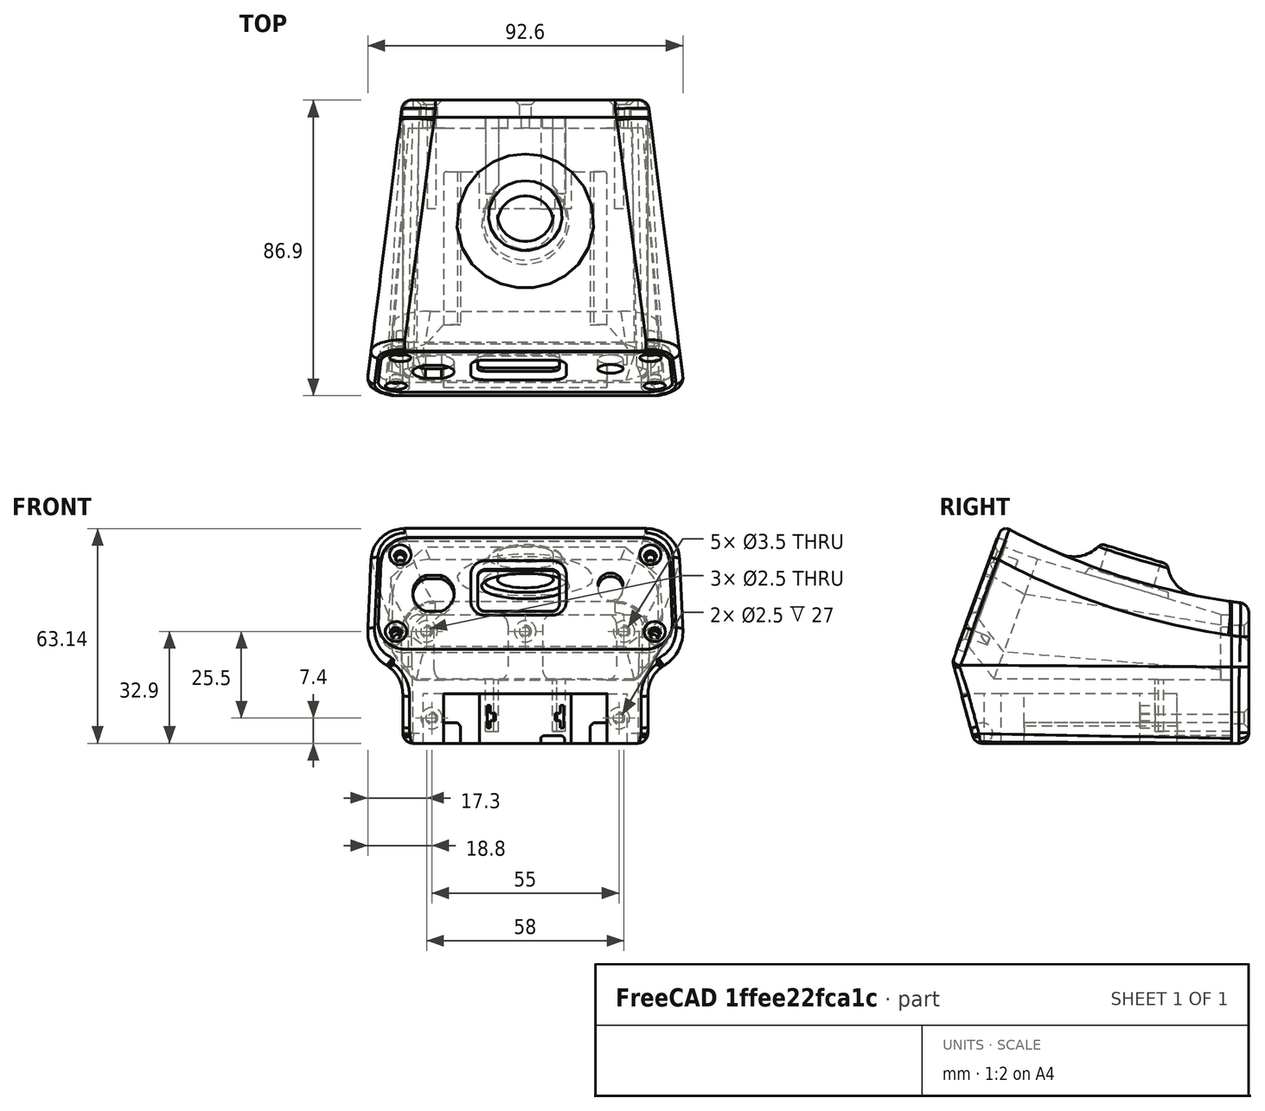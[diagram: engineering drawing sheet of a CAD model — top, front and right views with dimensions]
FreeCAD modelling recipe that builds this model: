
FCSTD DOCUMENT  (FreeCAD 2022.709R28846 (Git))
Label: solder_station4_snap
License: All rights reserved
LicenseURL: http://en.wikipedia.org/wiki/All_rights_reserved
objects: Sketcher::SketchObject×19, PartDesign::Pocket×9, PartDesign::Fillet×6, Mesh::Feature×4, Part::FeaturePython×3, App::DocumentObjectGroup×3, PartDesign::Chamfer×3, PartDesign::Body×3, PartDesign::FeatureBase×2, PartDesign::Pad×2, Spreadsheet::Sheet×1, Part::Plane×1, Part::Loft×1, Part::Extrusion×1, Part::MultiCommon×1, PartDesign::SubtractiveLoft×1, PartDesign::Revolution×1, PartDesign::Groove×1, App::Part×1
note: 102 computed .brp shape members not serialized (recipe doc carries the construction recipe); baked Part::Feature solids carry a one-line shape summary decoded from their .brp

FEATURE [Sketcher::SketchObject] Sketch  label="RearSupport"
  ArcFitTolerance = 0
  AttachmentOffset = pos=(0,0,-37.8) rot=(0,0,1;0rad)
  AttachmentSupport = -> [XZ_Plane005]
  FullyConstrained = true
  MapMode = 5
  Placement = pos=(0,37.8,8.4e-15) rot=(1,0,0;1.5708rad)
  Support = -> [XZ_Plane005]
  TreeRank = 0
  expr: AttachmentOffset.Base.z = -<<param>>.mid_depth / 2 + <<param>>.wall
  expr: Constraints[24] = 3
  expr: Constraints[37] = <<param>>.bottom_height
  expr: Constraints[38] = <<param>>.floor
  expr: Constraints[39] = <<param>>.rear_height - <<param>>.wall
  expr: Constraints[47] = <<param>>.reart_screw_width2
  expr: Constraints[48] = <<param>>.rear_screw_width1
  expr: Constraints[49] = <<param>>.screw_hole
  expr: Constraints[50] = <<param>>.rear_screw_height
  expr: Constraints[51] = <<param>>.rear_screw_height
  expr: Constraints[52] = <<param>>.rear_screw_offset
  sketch-geometry (22):
    g0: LineSegment StartX=-23.8 StartY=13.8 StartZ=0 EndX=-8.1 EndY=13.8 EndZ=0
    g1: LineSegment StartX=26.8 StartY=10.8 StartZ=0 EndX=26.8 EndY=-2.4 EndZ=0
    g2: LineSegment StartX=23.8 StartY=-5.4 StartZ=0 EndX=8.1 EndY=-5.4 EndZ=0
    g3: LineSegment StartX=-26.8 StartY=-2.4 StartZ=0 EndX=-26.8 EndY=10.8 EndZ=0
    g4: LineSegment StartX=-5.1 StartY=10.8 StartZ=0 EndX=-5.1 EndY=-2.4 EndZ=0
    g5: LineSegment StartX=5.1 StartY=10.8 StartZ=0 EndX=5.1 EndY=-2.4 EndZ=0
    g6: LineSegment StartX=8.1 StartY=13.8 StartZ=0 EndX=23.8 EndY=13.8 EndZ=0
    g7: LineSegment StartX=-8.1 StartY=-5.4 StartZ=0 EndX=-23.8 EndY=-5.4 EndZ=0
    g8: ArcOfCircle CenterX=-8.1 CenterY=10.8 CenterZ=0 NormalX=0 NormalY=0 NormalZ=1 AngleXU=0 Radius=3 StartAngle=0 EndAngle=1.5708
    g9: ArcOfCircle CenterX=8.1 CenterY=10.8 CenterZ=0 NormalX=0 NormalY=0 NormalZ=1 AngleXU=0 Radius=3 StartAngle=1.5708 EndAngle=3.14159
    g10: ArcOfCircle CenterX=-8.1 CenterY=-2.4 CenterZ=0 NormalX=0 NormalY=0 NormalZ=1 AngleXU=0 Radius=3 StartAngle=4.71239 EndAngle=6.28319
    g11: ArcOfCircle CenterX=8.1 CenterY=-2.4 CenterZ=0 NormalX=0 NormalY=0 NormalZ=1 AngleXU=0 Radius=3 StartAngle=3.14159 EndAngle=4.71239
    g12: ArcOfCircle CenterX=-23.8 CenterY=10.8 CenterZ=0 NormalX=0 NormalY=0 NormalZ=1 AngleXU=0 Radius=3 StartAngle=1.5708 EndAngle=3.14159
    g13: ArcOfCircle CenterX=-23.8 CenterY=-2.4 CenterZ=0 NormalX=0 NormalY=0 NormalZ=1 AngleXU=0 Radius=3 StartAngle=3.14159 EndAngle=4.71239
    g14: ArcOfCircle CenterX=23.8 CenterY=10.8 CenterZ=0 NormalX=0 NormalY=0 NormalZ=1 AngleXU=0 Radius=3 StartAngle=0 EndAngle=1.5708
    g15: ArcOfCircle CenterX=23.8 CenterY=-2.4 CenterZ=0 NormalX=0 NormalY=0 NormalZ=1 AngleXU=0 Radius=3 StartAngle=4.71239 EndAngle=6.28319
    g16: Circle [constr] CenterX=0 CenterY=-24 CenterZ=0 NormalX=0 NormalY=0 NormalZ=1 AngleXU=0 Radius=3
    g17: Circle CenterX=0 CenterY=8.9 CenterZ=0 NormalX=0 NormalY=0 NormalZ=1 AngleXU=0 Radius=1.25
    g18: Circle CenterX=-29 CenterY=8.9 CenterZ=0 NormalX=0 NormalY=0 NormalZ=1 AngleXU=0 Radius=1.25
    g19: Circle [constr] CenterX=-27.5 CenterY=-16.6 CenterZ=0 NormalX=0 NormalY=0 NormalZ=1 AngleXU=0 Radius=1.25
    g20: Circle [constr] CenterX=27.5 CenterY=-16.6 CenterZ=0 NormalX=0 NormalY=0 NormalZ=1 AngleXU=0 Radius=1.25
    g21: Circle CenterX=29 CenterY=8.9 CenterZ=0 NormalX=0 NormalY=0 NormalZ=1 AngleXU=0 Radius=1.25
  constraints (53):
    c: Horizontal(g0)
    c: Horizontal(g2)
    c: Vertical(g1)
    c: Vertical(g3)
    c: Vertical(g4)
    c: Vertical(g5)
    c: Tangent(g0,g6)
    c: Tangent(g2,g7)
    c: Tangent(g0,g8) = 1.5708
    c: Tangent(g4,g8) = 1.5708
    c: Tangent(g5,g9) = -1.5708
    c: Tangent(g6,g9) = 1.5708
    c: Tangent(g7,g10) = 1.5708
    c: Tangent(g4,g10) = 1.5708
    c: Tangent(g5,g11) = -1.5708
    c: Tangent(g2,g11) = 1.5708
    c: Tangent(g0,g12) = 1.5708
    c: Tangent(g3,g12) = 1.5708
    c: Tangent(g3,g13) = 1.5708
    c: Tangent(g7,g13) = 1.5708
    c: Tangent(g6,g14) = 1.5708
    c: Tangent(g1,g14) = 1.5708
    c: Tangent(g1,g15) = 1.5708
    c: Tangent(g2,g15) = 1.5708
    c: Radius(g9) = 3
    c: Equal(g12,g13)
    c: Equal(g13,g10)
    c: Equal(g10,g8)
    c: Equal(g11,g15)
    c: Equal(g15,g14)
    c: Equal(g14,g9)
    c: DistanceX(g4,g-1) = 5.1
    c: DistanceX(g5,g1) = 21.7
    c: Symmetric(g4,g5,g-2)
    c: Equal(g7,g2)
    c: PointOnObject(g16,g-2)
    c: Radius(g16) = 3
    c: DistanceY(g16,g-1) = 24
    c: DistanceY(g16,g2) = 18.6
    c: DistanceY(g16,g6) = 37.8
    c: PointOnObject(g17,g-2)
    c: Equal(g21,g18)
    c: Equal(g18,g19)
    c: Equal(g19,g20)
    c: Equal(g18,g17)
    c: Symmetric(g20,g19,g-2)
    c: Symmetric(g18,g21,g-2)
    c: DistanceX(g19,g20) = 55
    c: DistanceX(g18,g21) = 58
    c: Diameter(g19) = 2.5
    c: DistanceY(g20,g21) = 25.5
    c: DistanceY(g20,g17) = 25.5
    c: DistanceY(g16,g19) = 7.4
FEATURE [Spreadsheet::Sheet] Spreadsheet  label="param"
  PythonMode = false
  ShowCells = 0
  TreeRank = 0
  cells = A1=Body; B2=top_depth; C2(top_depth)=70; B3=mid_depth; C3(mid_depth)=82; D3=half is rear reference; B4=bottom_depth; C4(bottom_depth)=75; B6=bottom_width; C6(bottom_width)=72; B7=bottom_height; C7(bottom_height)=24; B8=bottom_angle; C8(bottom_angle)=15; B10=rear_width; C10(rear_width)=72; B11=rear_height; C11(rear_height)=41; B13=mid_width; C13(mid_width)=80; B14=mid_height; C14(mid_height)=50; B16=front_width1; C16(front_width1)=91; D16=@top; E16=upper; B17=front_width2; C17(front_width2)=94; D17=@mid; E17=lower; B18=front_height; C18(front_height)=64; B19=front_angle; C19(front_angle)=20; D19=20 is actual value; B21=wall; C21(wall)=3.2; B22=radius_big; C22(radius_big)=10; B23=radius_small; C23(radius_small)=3; B24=arch; C24(arch)=200; A26=Button; B27=button_offset; C27(button_offset)=10; B28=button_inside_dia; C28(button_inside_dia)=20; B29=button_outside_dia; C29(button_outside_dia)=22; B30=button_height; C30(button_height)=24; B31=button_extension; C31(button_extension)=8; B32=button_fillet; C32(button_fillet)=12; B33=button_angle; C33(button_angle)=-17; B34=button_hole; C34(button_hole)=16.4; B35=button_hole_center; C35(button_hole_center)=-0.5; A37=Battery Cuts; B38=batt_carveout; C38(batt_carveout)=14.6; B39=batt_rail; C39(batt_rail)=6; B40=batt_rail_length; C40(batt_rail_length)=45; A42=Terminals; B43=terminal_height; C43(terminal_height)=6.6; B44=terminal_thickness; C44(terminal_thickness)=1; B45=terminal_seperation; C45(terminal_seperation)=21.5; B46=terminal_offset; C46(terminal_offset)=4.5; B47=terminal_depth; C47(terminal_depth)=22.5; A49=Box Interior; B50=floor; C50(floor)=18.6; B51=rear_inside_width; C51(rear_inside_width)==C10 - C21; D51=calc; B52=rear_inside_height; C52(rear_inside_height)==C11 - C21; D52=calc; B53=mid_inside_width; C53(mid_inside_width)==C13; D53=calc; B54=mid_inside_height; C54(mid_inside_height)==C14 + 6; D54=calc; B55=front_inside_width1; C55(front_inside_width1)==C62 - C58 * 2; D55=calc; E55=upper; B56=front_inside_width2; C56(front_inside_width2)==C63 - C58 * 2; D56=calc; E56=lower; B57=front_inside_height; C57(front_inside_height)==C64 - C59 * 2; D57=calc; B58=front_width_lip_width; C58(front_width_lip_width)=3; B59=front_inside_lip_height; C59(front_inside_lip_height)=2; A61=Face; B62=face_width1; C62(face_width1)==84 + 1; B63=face_width2; C63(face_width2)==85.5 + 1; B64=face_height; C64(face_height)==34 + 1; B65=face_thickness; C65(face_thickness)=3; B66=face_radius; C66(face_radius)=8; B67=face_offset; C67(face_offset)=2.8; D67=2.8; A69=Screws; B70=screw_hole; C70(screw_hole)=2.5; B72=front_screw_width1; C72(front_screw_width1)=73.5; D72=upper; B73=front_screw_width2; C73(front_screw_width2)=76; D73=lower; B74=front_screw_height; C74(front_screw_height)=24; B75=front_screw_offset; C75(front_screw_offset)=5.5; B77=rear_screw_width1; C77(rear_screw_width1)=58; B78=reart_screw_width2; C78(reart_screw_width2)=55; B79=rear_screw_height; C79(rear_screw_height)=25.5; B80=rear_screw_offset; C80(rear_screw_offset)=7.4; A82=Back; B83=back_thickness; C83(back_thickness)=5
FEATURE [Sketcher::SketchObject] Sketch008  label="SketchButtonHole"
  ArcFitTolerance = 0
  AttachmentOffset = pos=(0,-0.5,24) rot=(1,0,0;-0.296706rad)
  AttachmentSupport = -> [XY_Plane005]
  FullyConstrained = true
  MapMode = 5
  Placement = pos=(0,-0.5,24) rot=(1,0,0;5.98648rad)
  Support = -> [XY_Plane005]
  TreeRank = 0
  expr: AttachmentOffset.Base.y = <<param>>.button_hole_center
  expr: AttachmentOffset.Base.z = <<param>>.button_height
  expr: AttachmentOffset.Rotation.Angle = <<param>>.button_angle
  expr: Constraints[0] = <<param>>.button_hole
  expr: Constraints[2] = <<param>>.button_offset
  sketch-geometry (1):
    g0: Circle CenterX=0 CenterY=10 CenterZ=0 NormalX=0 NormalY=0 NormalZ=1 AngleXU=0 Radius=8.2
  constraints (3):
    c: Diameter(g0) = 16.4
    c: PointOnObject(g0,g-2)
    c: DistanceY(g-1,g0) = 10
FEATURE [Sketcher::SketchObject] Sketch012  label="SketchSide"
  ArcFitTolerance = 0
  AttachmentOffset = pos=(2.5,0,0) rot=(0,0,1;0rad)
  AttachmentSupport = -> [YZ_Plane006]
  FullyConstrained = true
  MapMode = 5
  Placement = pos=(6e-16,2.5,-6e-16) rot=(0.57735,0.57735,0.57735;2.0944rad)
  Support = -> [YZ_Plane006]
  TreeRank = 0
  expr: AttachmentOffset.Base.x = <<param>>.back_thickness / 2
  expr: Constraints[14] = <<param>>.bottom_height
  expr: Constraints[15] = <<param>>.radius_small
  expr: Constraints[16] = 90 - <<param>>.bottom_angle
  expr: Constraints[17] = 90 - <<param>>.front_angle
  expr: Constraints[21] = <<param>>.front_height
  expr: Constraints[4] = <<param>>.rear_height - <<param>>.bottom_height
  expr: Constraints[5] = <<param>>.arch
  expr: Constraints[6] = <<param>>.mid_depth + <<param>>.back_thickness
  sketch-geometry (7):
    g0: LineSegment StartX=43.5 StartY=0 StartZ=0 EndX=43.5 EndY=17 EndZ=0
    g1: LineSegment StartX=-43.5 StartY=0 StartZ=0 EndX=-28.9412 EndY=40 EndZ=0
    g2: ArcOfCircle CenterX=66.6993 CenterY=215.65 CenterZ=0 NormalX=0 NormalY=0 NormalZ=1 AngleXU=0 Radius=200 StartAngle=4.21378 EndAngle=4.59613
    g3: LineSegment StartX=-43.5 StartY=0 StartZ=0 EndX=-37.665 EndY=-21.7764 EndZ=0
    g4: LineSegment StartX=-34.7672 StartY=-24 StartZ=0 EndX=43.5 EndY=-24 EndZ=0
    g5: LineSegment StartX=43.5 StartY=-24 StartZ=0 EndX=43.5 EndY=0 EndZ=0
    g6: ArcOfCircle CenterX=-34.7672 CenterY=-21 CenterZ=0 NormalX=0 NormalY=0 NormalZ=1 AngleXU=0 Radius=3 StartAngle=3.40338 EndAngle=4.71239
  constraints (22):
    c: PointOnObject(g1,g-1)
    c: Vertical(g0)
    c: Coincident(g2,g0)
    c: Symmetric(g1,g0,g-2)
    c: DistanceY(g0,g0) = 17
    c: Radius(g2) = 200
    c: DistanceX(g1,g0) = 87
    c: Horizontal(g4)
    c: Coincident(g5,g4)
    c: Vertical(g5)
    c: Coincident(g6,g3)
    c: Coincident(g6,g4)
    c: Tangent(g6,g4)
    c: Tangent(g6,g3)
    c: DistanceY(g4,g-1) = 24
    c: Radius(g6) = 3
    c: Angle(g3,g-1) = 1.309
    c: Angle(g-1,g1) = 1.22173
    c: Coincident(g3,g1)
    c: Coincident(g5,g0)
    c: Coincident(g2,g1)
    c: DistanceY(g4,g1) = 64
FEATURE [Sketcher::SketchObject] Sketch018  label="SketchBat1"
  ArcFitTolerance = 0
  AttachmentOffset = pos=(0,0,-24) rot=(0,0,1;0rad)
  AttachmentSupport = -> [XY_Plane005]
  FullyConstrained = true
  MapMode = 5
  Placement = pos=(0,0,-24) rot=(0,0,1;0rad)
  Support = -> [XY_Plane005]
  TreeRank = 0
  expr: AttachmentOffset.Base.z = -<<param>>.bottom_height
  expr: Constraints[63] = <<param>>.batt_rail_length
  expr: Constraints[64] = <<param>>.mid_depth / 2
  sketch-geometry (21):
    g0: LineSegment StartX=-24 StartY=-41.7082 StartZ=0 EndX=24 EndY=-41.7082 EndZ=0
    g1: LineSegment StartX=24 StartY=-41.7082 StartZ=0 EndX=24 EndY=-31.7082 EndZ=0
    g2: LineSegment StartX=24 StartY=-31.7082 StartZ=0 EndX=30 EndY=-31.7082 EndZ=0
    g3: LineSegment StartX=30 StartY=-31.7082 StartZ=0 EndX=30 EndY=-26.7082 EndZ=0
    g4: LineSegment StartX=30 StartY=-26.7082 StartZ=0 EndX=24 EndY=-20 EndZ=0
    g5: LineSegment StartX=24 StartY=-20 StartZ=0 EndX=24 EndY=24 EndZ=0
    g6: LineSegment StartX=13.5 StartY=24 StartZ=0 EndX=13.5 EndY=14 EndZ=0
    g7: LineSegment StartX=13.5 StartY=14 StartZ=0 EndX=-13.5 EndY=14 EndZ=0
    g8: LineSegment StartX=-13.5 StartY=14 StartZ=0 EndX=-13.5 EndY=24 EndZ=0
    g9: LineSegment StartX=-24 StartY=24 StartZ=0 EndX=-24 EndY=-20 EndZ=0
    g10: LineSegment StartX=-24 StartY=-20 StartZ=0 EndX=-30 EndY=-26.7082 EndZ=0
    g11: LineSegment StartX=-30 StartY=-26.7082 StartZ=0 EndX=-30 EndY=-31.7082 EndZ=0
    g12: LineSegment StartX=-30 StartY=-31.7082 StartZ=0 EndX=-24 EndY=-31.7082 EndZ=0
    g13: LineSegment StartX=-24 StartY=-31.7082 StartZ=0 EndX=-24 EndY=-41.7082 EndZ=0
    g14: Circle [constr] CenterX=0 CenterY=41 CenterZ=0 NormalX=0 NormalY=0 NormalZ=1 AngleXU=0 Radius=4
    g15: ArcOfCircle CenterX=-14.5 CenterY=24 CenterZ=0 NormalX=0 NormalY=0 NormalZ=1 AngleXU=0 Radius=1 StartAngle=6.28318 EndAngle=7.85399
    g16: LineSegment StartX=-23 StartY=25 StartZ=0 EndX=-14.5 EndY=25 EndZ=0
    g17: LineSegment StartX=14.5 StartY=25 StartZ=0 EndX=23 EndY=25 EndZ=0
    g18: ArcOfCircle CenterX=-23 CenterY=24 CenterZ=0 NormalX=0 NormalY=0 NormalZ=1 AngleXU=0 Radius=1 StartAngle=1.57079 EndAngle=3.1416
    g19: ArcOfCircle CenterX=14.5 CenterY=24 CenterZ=0 NormalX=0 NormalY=0 NormalZ=1 AngleXU=0 Radius=1 StartAngle=1.5708 EndAngle=3.14159
    g20: ArcOfCircle CenterX=23 CenterY=24 CenterZ=0 NormalX=0 NormalY=0 NormalZ=1 AngleXU=0 Radius=1.00001 StartAngle=2.75124e-06 EndAngle=1.5708
  constraints (65):
    c: Horizontal(g0)
    c: Coincident(g1,g0)
    c: Vertical(g1)
    c: Coincident(g2,g1)
    c: Horizontal(g2)
    c: Coincident(g3,g2)
    c: Coincident(g3,g4)
    c: Vertical(g5)
    c: Coincident(g6,g7)
    c: Coincident(g7,g8)
    c: Vertical(g8)
    c: Vertical(g9)
    c: Coincident(g10,g11)
    c: Vertical(g11)
    c: Coincident(g11,g12)
    c: Horizontal(g12)
    c: Coincident(g12,g13)
    c: Equal(g6,g8)
    c: Equal(g5,g9)
    c: Equal(g4,g10)
    c: Equal(g3,g11)
    c: Equal(g12,g2)
    c: Equal(g1,g13)
    c: Coincident(g13,g0)
    c: Vertical(g13)
    c: DistanceX(g7,g7) = 27
    c: Symmetric(g7,g6,g-2)
    c: Distance(g4) = 9
    c: Vertical(g3)
    c: DistanceY(g3,g3) = 5
    c: DistanceX(g2,g2) = 6
    c: DistanceY(g1,g1) = 10
    c: DistanceX(g0,g0) = 48
    c: PointOnObject(g14,g-2)
    c: Coincident(g9,g10)
    c: Coincident(g5,g4)
    c: Coincident(g15,g8)
    c: Coincident(g16,g15)
    c: Tangent(g15,g8)
    c: Horizontal(g16)
    c: Horizontal(g17)
    c: DistanceX(g9,g5) = 48
    c: Symmetric(g4,g9,g-2)
    c: Equal(g16,g17)
    c: Coincident(g18,g9)
    c: Coincident(g18,g16)
    c: Equal(g18,g15)
    c: Tangent(g18,g16)
    c: Tangent(g18,g9)
    c: DistanceY(g6,g17) = 11
    c: Vertical(g6)
    c: Coincident(g19,g6)
    c: Coincident(g19,g17)
    c: Coincident(g20,g17)
    c: Coincident(g20,g5)
    c: Tangent(g20,g17)
    c: Tangent(g20,g5)
    c: Tangent(g19,g6)
    c: Tangent(g19,g17)
    c: Equal(g15,g19)
    c: Radius(g19) = 1
    c: Radius(g14) = 4
    c: DistanceY(g15,g14) = 16
    c: DistanceY(g9,g16) = 45
    c: DistanceY(g-1,g14) = 41
FEATURE [Sketcher::SketchObject] Sketch019  label="SketchBat2"
  ArcFitTolerance = 0
  AttachmentOffset = pos=(0,0,-25) rot=(0,0,1;0rad)
  AttachmentSupport = -> [XZ_Plane005]
  FullyConstrained = true
  MapMode = 5
  Placement = pos=(0,25,5.6e-15) rot=(1,0,0;1.5708rad)
  Support = -> [XZ_Plane005]
  TreeRank = 0
  expr: AttachmentOffset.Base.z = -<<param>>.mid_depth / 2 + 16
  expr: Constraints[17] = <<param>>.bottom_height
  expr: Constraints[18] = <<param>>.batt_rail
  expr: Constraints[19] = 48.01mm
  sketch-geometry (10):
    g0: LineSegment StartX=-24.005 StartY=-18 StartZ=0 EndX=-20.005 EndY=-18 EndZ=0
    g1: LineSegment StartX=-19.005 StartY=-24 StartZ=0 EndX=-24.005 EndY=-24 EndZ=0
    g2: LineSegment StartX=-24.005 StartY=-24 StartZ=0 EndX=-24.005 EndY=-18 EndZ=0
    g3: LineSegment StartX=24.005 StartY=-18 StartZ=0 EndX=20.005 EndY=-18 EndZ=0
    g4: LineSegment StartX=19.005 StartY=-24 StartZ=0 EndX=24.005 EndY=-24 EndZ=0
    g5: LineSegment StartX=24.005 StartY=-24 StartZ=0 EndX=24.005 EndY=-18 EndZ=0
    g6: LineSegment StartX=-19.005 StartY=-19 StartZ=0 EndX=-19.005 EndY=-24 EndZ=0
    g7: LineSegment StartX=19.005 StartY=-24 StartZ=0 EndX=19.005 EndY=-19 EndZ=0
    g8: LineSegment StartX=-20.005 StartY=-18 StartZ=0 EndX=-19.005 EndY=-19 EndZ=0
    g9: LineSegment StartX=19.005 StartY=-19 StartZ=0 EndX=20.005 EndY=-18 EndZ=0
  constraints (29):
    c: Coincident(g1,g2)
    c: Coincident(g2,g0)
    c: Horizontal(g0)
    c: Horizontal(g1)
    c: Vertical(g2)
    c: Coincident(g4,g5)
    c: Coincident(g5,g3)
    c: Horizontal(g3)
    c: Horizontal(g4)
    c: Vertical(g5)
    c: Coincident(g6,g1)
    c: Vertical(g6)
    c: Equal(g1,g4)
    c: Coincident(g7,g4)
    c: Vertical(g7)
    c: Equal(g6,g7)
    c: Symmetric(g1,g4,g-2)
    c: DistanceY(g1,g-1) = 24
    c: DistanceY(g4,g3) = 6
    c: DistanceX(g1,g4) = 48.01
    c: DistanceX(g4,g4) = 5
    c: Coincident(g8,g0)
    c: Coincident(g8,g6)
    c: Coincident(g9,g7)
    c: Coincident(g9,g3)
    c: Equal(g0,g3)
    c: Equal(g2,g5)
    c: DistanceX(g0,g0) = 4
    c: DistanceY(g1,g6) = 5
FEATURE [Sketcher::SketchObject] Sketch021  label="SketchButton"
  ArcFitTolerance = 0
  AttachmentOffset = pos=(10,24,0) rot=(0,0,1;-0.296706rad)
  AttachmentSupport = -> [YZ_Plane005]
  FullyConstrained = true
  MapMode = 5
  Placement = pos=(-3.1e-15,10,24) rot=(-0.51122,-0.690875,-0.51122;4.35074rad)
  Support = -> [YZ_Plane005]
  TreeRank = 0
  expr: AttachmentOffset.Base.x = <<param>>.button_offset
  expr: AttachmentOffset.Base.y = <<param>>.button_height
  expr: AttachmentOffset.Rotation.Angle = <<param>>.button_angle
  expr: Constraints[6] = <<param>>.button_extension
  expr: Constraints[7] = <<param>>.button_outside_dia / 2
  sketch-geometry (5):
    g0: LineSegment StartX=0 StartY=0 StartZ=0 EndX=0 EndY=8 EndZ=0
    g1: LineSegment StartX=0 StartY=8 StartZ=0 EndX=9 EndY=8 EndZ=0
    g2: LineSegment StartX=0 StartY=0 StartZ=0 EndX=11 EndY=0 EndZ=0
    g3: LineSegment StartX=11 StartY=0 StartZ=0 EndX=11 EndY=6 EndZ=0
    g4: ArcOfCircle CenterX=9 CenterY=6 CenterZ=0 NormalX=0 NormalY=0 NormalZ=1 AngleXU=0 Radius=2 StartAngle=1.123e-13 EndAngle=1.5708
  constraints (13):
    c: Coincident(g0,g-1)
    c: PointOnObject(g0,g-2)
    c: Coincident(g1,g0)
    c: Horizontal(g1)
    c: Coincident(g2,g0)
    c: Horizontal(g2)
    c: DistanceY(g0,g0) = 8
    c: DistanceX(g2,g2) = 11
    c: Coincident(g3,g2)
    c: Vertical(g3)
    c: Radius(g4) = 2
    c: Tangent(g4,g3) = -1.5708
    c: Tangent(g4,g1) = 1.5708
FEATURE [Sketcher::SketchObject] Sketch022  label="SketchRearInside"
  ArcFitTolerance = 0
  AttachmentOffset = pos=(0,0,-37.8) rot=(0,0,1;0rad)
  AttachmentSupport = -> [XZ_Plane005]
  FullyConstrained = true
  MapMode = 5
  Placement = pos=(0,37.8,8.4e-15) rot=(1,0,0;1.5708rad)
  Support = -> [XZ_Plane005]
  TreeRank = 0
  expr: AttachmentOffset.Base.z = -<<param>>.mid_depth / 2 + <<param>>.wall
  expr: Constraints[12] = <<param>>.radius_small
  expr: Constraints[18] = <<param>>.rear_inside_width
  expr: Constraints[26] = <<param>>.bottom_height
  expr: Constraints[27] = <<param>>.rear_inside_height
  expr: Constraints[29] = <<param>>.floor
  sketch-geometry (9):
    g0: LineSegment StartX=-34.4 StartY=10.8 StartZ=0 EndX=-34.4 EndY=-2.39998 EndZ=0
    g1: LineSegment StartX=-31.4 StartY=-5.4 StartZ=0 EndX=31.4 EndY=-5.4 EndZ=0
    g2: LineSegment StartX=34.4 StartY=-2.39998 StartZ=0 EndX=34.4 EndY=10.8 EndZ=0
    g3: LineSegment StartX=-31.4 StartY=13.8 StartZ=0 EndX=31.4 EndY=13.8 EndZ=0
    g4: ArcOfCircle CenterX=31.4 CenterY=10.8 CenterZ=0 NormalX=0 NormalY=0 NormalZ=1 AngleXU=0 Radius=3 StartAngle=6.28318 EndAngle=7.85399
    g5: ArcOfCircle CenterX=31.4 CenterY=-2.4 CenterZ=0 NormalX=0 NormalY=0 NormalZ=1 AngleXU=0 Radius=3 StartAngle=4.71238 EndAngle=6.28319
    g6: ArcOfCircle CenterX=-31.4 CenterY=10.8 CenterZ=0 NormalX=0 NormalY=0 NormalZ=1 AngleXU=0 Radius=3 StartAngle=1.57079 EndAngle=3.1416
    g7: ArcOfCircle CenterX=-31.4 CenterY=-2.4 CenterZ=0 NormalX=0 NormalY=0 NormalZ=1 AngleXU=0 Radius=3 StartAngle=3.14159 EndAngle=4.71239
    g8: Circle [constr] CenterX=0 CenterY=-24 CenterZ=0 NormalX=0 NormalY=0 NormalZ=1 AngleXU=0 Radius=3
  constraints (30):
    c: Vertical(g0)
    c: Horizontal(g1)
    c: Vertical(g2)
    c: Horizontal(g3)
    c: Equal(g3,g1)
    c: Equal(g0,g2)
    c: Coincident(g4,g3)
    c: Coincident(g4,g2)
    c: Coincident(g5,g2)
    c: Coincident(g5,g1)
    c: Coincident(g6,g0)
    c: Coincident(g6,g3)
    c: Radius(g6) = 3
    c: Equal(g6,g4)
    c: Equal(g4,g5)
    c: Coincident(g7,g1)
    c: Coincident(g7,g0)
    c: Equal(g5,g7)
    c: DistanceX(g0,g2) = 68.8
    c: Symmetric(g0,g2,g-2)
    c: Tangent(g4,g2)
    c: Tangent(g4,g3)
    c: Tangent(g5,g2)
    c: Tangent(g5,g1)
    c: Tangent(g6,g3)
    c: PointOnObject(g8,g-2)
    c: DistanceY(g8,g-1) = 24
    c: DistanceY(g8,g3) = 37.8
    c: Radius(g8) = 3
    c: DistanceY(g8,g1) = 18.6
FEATURE [Sketcher::SketchObject] Sketch023  label="SketchFrontInside"
  ArcFitTolerance = 0
  AttachmentOffset = pos=(0,0,38) rot=(1,0,0;-0.349066rad)
  AttachmentSupport = -> [XZ_Plane005]
  FullyConstrained = true
  MapMode = 5
  Placement = pos=(0,-38,-8.4e-15) rot=(-1,0,0;5.06145rad)
  Support = -> [XZ_Plane005]
  TreeRank = 0
  expr: AttachmentOffset.Base.z = <<param>>.mid_depth / 2 - <<param>>.face_thickness
  expr: AttachmentOffset.Rotation.Angle = -<<param>>.front_angle
  expr: Constraints[19] = <<param>>.front_inside_width2
  expr: Constraints[1] = <<param>>.front_inside_width1
  expr: Constraints[20] = <<param>>.front_inside_width2 / 2
  expr: Constraints[21] = <<param>>.face_offset + <<param>>.front_inside_lip_height
  expr: Constraints[2] = <<param>>.front_inside_height
  sketch-geometry (8):
    g0: LineSegment StartX=-29.5 StartY=4.8 StartZ=0 EndX=29.5 EndY=4.8 EndZ=0
    g1: LineSegment StartX=29.5 StartY=35.8 StartZ=0 EndX=-29.5 EndY=35.8 EndZ=0
    g2: LineSegment StartX=-39.5 StartY=26.3677 StartZ=0 EndX=-40.25 EndY=13.3677 EndZ=0
    g3: LineSegment StartX=-39.5 StartY=26.3677 StartZ=0 EndX=-29.5 EndY=35.8 EndZ=0
    g4: LineSegment StartX=29.5 StartY=35.8 StartZ=0 EndX=39.5 EndY=26.3677 EndZ=0
    g5: LineSegment StartX=40.25 StartY=13.3677 StartZ=0 EndX=29.5 EndY=4.8 EndZ=0
    g6: LineSegment StartX=-40.25 StartY=13.3677 StartZ=0 EndX=-29.5 EndY=4.8 EndZ=0
    g7: LineSegment StartX=39.5 StartY=26.3677 StartZ=0 EndX=40.25 EndY=13.3677 EndZ=0
  constraints (22):
    c: Symmetric(g0,g0,g-2)
    c: DistanceX(g2,g4) = 79
    c: DistanceY(g0,g1) = 31
    c: Symmetric(g1,g1,g-2)
    c: Coincident(g3,g2)
    c: Coincident(g3,g1)
    c: Coincident(g4,g1)
    c: Coincident(g5,g0)
    c: Coincident(g6,g2)
    c: Coincident(g6,g0)
    c: Equal(g3,g6)
    c: Equal(g6,g5)
    c: Equal(g5,g4)
    c: Coincident(g7,g4)
    c: Coincident(g7,g5)
    c: DistanceY(g7,g7) = 13
    c: Equal(g7,g2)
    c: Equal(g1,g0)
    c: DistanceX(g1,g1) = 59
    c: DistanceX(g2,g5) = 80.5
    c: DistanceX(g2,g-1) = 40.25
    c: DistanceY(g-1,g0) = 4.8
FEATURE [Sketcher::SketchObject] Sketch024  label="SketchFaceCut"
  ArcFitTolerance = 0
  AttachmentOffset = pos=(0,0,38) rot=(1,0,0;-0.349066rad)
  AttachmentSupport = -> [XZ_Plane005]
  FullyConstrained = true
  MapMode = 5
  Placement = pos=(0,-38,-8.4e-15) rot=(-1,0,0;5.06145rad)
  Support = -> [XZ_Plane005]
  TreeRank = 0
  expr: AttachmentOffset.Base.z = <<param>>.mid_depth / 2 - <<param>>.face_thickness
  expr: AttachmentOffset.Rotation.Angle = -<<param>>.front_angle
  expr: Constraints[13] = <<param>>.face_radius
  expr: Constraints[22] = <<param>>.face_width1
  expr: Constraints[23] = <<param>>.face_width2
  expr: Constraints[24] = <<param>>.face_offset
  expr: Constraints[25] = <<param>>.face_height
  sketch-geometry (8):
    g0: LineSegment StartX=-34.5062 StartY=37.8 StartZ=0 EndX=34.5063 EndY=37.8 EndZ=0
    g1: LineSegment StartX=42.5001 StartY=30.1155 StartZ=0 EndX=43.25 EndY=11.1155 EndZ=0
    g2: LineSegment StartX=35.2562 StartY=2.8 StartZ=0 EndX=-35.2562 EndY=2.8 EndZ=0
    g3: LineSegment StartX=-43.25 StartY=11.1156 StartZ=0 EndX=-42.4999 EndY=30.1156 EndZ=0
    g4: ArcOfCircle CenterX=34.5063 CenterY=29.8 CenterZ=0 NormalX=0 NormalY=0 NormalZ=1 AngleXU=0 Radius=8 StartAngle=0.0394514 EndAngle=1.5708
    g5: ArcOfCircle CenterX=35.2563 CenterY=10.8 CenterZ=0 NormalX=0 NormalY=0 NormalZ=1 AngleXU=0 Radius=8 StartAngle=4.71239 EndAngle=6.32264
    g6: ArcOfCircle CenterX=-34.5062 CenterY=29.8 CenterZ=0 NormalX=0 NormalY=0 NormalZ=1 AngleXU=0 Radius=8 StartAngle=1.5708 EndAngle=3.10214
    g7: ArcOfCircle CenterX=-35.2562 CenterY=10.8 CenterZ=0 NormalX=0 NormalY=0 NormalZ=1 AngleXU=0 Radius=8 StartAngle=3.10214 EndAngle=4.71239
  constraints (27):
    c: Horizontal(g0)
    c: Coincident(g4,g0)
    c: Coincident(g4,g1)
    c: Coincident(g5,g1)
    c: Coincident(g5,g2)
    c: Coincident(g6,g0)
    c: Coincident(g6,g3)
    c: Coincident(g7,g3)
    c: Coincident(g7,g2)
    c: Equal(g1,g3)
    c: Equal(g4,g6)
    c: Equal(g6,g7)
    c: Equal(g7,g5)
    c: Radius(g4) = 8
    c: Tangent(g6,g3)
    c: Tangent(g7,g3)
    c: Tangent(g7,g2)
    c: Tangent(g6,g0)
    c: Tangent(g4,g0)
    c: Tangent(g4,g1)
    c: Tangent(g5,g1)
    c: Tangent(g5,g2)
    c: DistanceX(g3,g1) = 85
    c: DistanceX(g3,g1) = 86.5
    c: DistanceY(g-1,g2) = 2.8
    c: DistanceY(g2,g0) = 35
    c: Symmetric(g2,g2,g-2)
FEATURE [Sketcher::SketchObject] Sketch025  label="SketchMidInside"
  ArcFitTolerance = 0
  AttachmentOffset = pos=(0,0,27) rot=(1,0,0;-0.349066rad)
  AttachmentSupport = -> [XZ_Plane005]
  FullyConstrained = true
  MapMode = 5
  Placement = pos=(0,-27,-6e-15) rot=(-1,0,0;5.06145rad)
  Support = -> [XZ_Plane005]
  TreeRank = 0
  expr: AttachmentOffset.Base.z = <<param>>.mid_depth / 2 - 14
  expr: AttachmentOffset.Rotation.Angle = -<<param>>.front_angle
  expr: Constraints[10] = <<param>>.radius_big + 1
  expr: Constraints[11] = <<param>>.floor
  expr: Constraints[12] = Spreadsheet.mid_inside_width - 2
  expr: Constraints[14] = <<param>>.mid_inside_height
  expr: Constraints[23] = <<param>>.mid_width - 16
  expr: Constraints[4] = <<param>>.bottom_height
  sketch-geometry (9):
    g0: LineSegment StartX=-28 StartY=32 StartZ=0 EndX=28 EndY=32 EndZ=0
    g1: LineSegment StartX=39 StartY=21 StartZ=0 EndX=39 EndY=3 EndZ=0
    g2: LineSegment StartX=32 StartY=-5.4 StartZ=0 EndX=-32 EndY=-5.4 EndZ=0
    g3: LineSegment StartX=-39 StartY=3 StartZ=0 EndX=-39 EndY=21 EndZ=0
    g4: Circle [constr] CenterX=0 CenterY=-24 CenterZ=0 NormalX=0 NormalY=0 NormalZ=1 AngleXU=0 Radius=3
    g5: ArcOfCircle CenterX=-28 CenterY=21 CenterZ=0 NormalX=0 NormalY=0 NormalZ=1 AngleXU=0 Radius=11 StartAngle=1.5708 EndAngle=3.14159
    g6: ArcOfCircle CenterX=28 CenterY=21 CenterZ=0 NormalX=0 NormalY=0 NormalZ=1 AngleXU=0 Radius=11 StartAngle=0 EndAngle=1.5708
    g7: ArcOfCircle CenterX=-17.5474 CenterY=13.7605 CenterZ=0 NormalX=0 NormalY=0 NormalZ=1 AngleXU=0 Radius=24 StartAngle=3.60651 EndAngle=4.06615
    g8: ArcOfCircle CenterX=17.5474 CenterY=13.7605 CenterZ=0 NormalX=0 NormalY=0 NormalZ=1 AngleXU=0 Radius=24 StartAngle=5.35863 EndAngle=5.81826
  constraints (25):
    c: Vertical(g1)
    c: Vertical(g3)
    c: PointOnObject(g4,g-2)
    c: Radius(g4) = 3
    c: DistanceY(g4,g-1) = 24
    c: Tangent(g3,g5) = 1.5708
    c: Tangent(g0,g5) = 1.5708
    c: Tangent(g0,g6) = 1.5708
    c: Tangent(g1,g6) = 1.5708
    c: Equal(g6,g5)
    c: Radius(g6) = 11
    c: DistanceY(g4,g2) = 18.6
    c: DistanceX(g3,g1) = 78
    c: Symmetric(g2,g2,g-2)
    c: DistanceY(g4,g0) = 56
    c: Symmetric(g0,g0,g-2)
    c: Equal(g3,g1)
    c: Coincident(g7,g2)
    c: Coincident(g8,g1)
    c: Coincident(g8,g2)
    c: Coincident(g7,g3)
    c: Equal(g8,g7)
    c: Radius(g8) = 24
    c: DistanceX(g2,g2) = 64
    c: DistanceY(g1,g1) = 18
FEATURE [Sketcher::SketchObject] Sketch026  label="SketchFrontScrews"
  ArcFitTolerance = 0
  AttachmentOffset = pos=(0,0,38) rot=(1,0,0;-0.349066rad)
  AttachmentSupport = -> [XZ_Plane005]
  FullyConstrained = true
  MapMode = 5
  Placement = pos=(0,-38,-8.4e-15) rot=(-1,0,0;5.06145rad)
  Support = -> [XZ_Plane005]
  TreeRank = 0
  expr: AttachmentOffset.Base.z = <<param>>.mid_depth / 2 - <<param>>.face_thickness
  expr: AttachmentOffset.Rotation.Angle = -<<param>>.front_angle
  expr: Constraints[0] = <<param>>.front_screw_width1
  expr: Constraints[13] = <<param>>.screw_hole
  expr: Constraints[1] = <<param>>.front_screw_width2
  expr: Constraints[2] = <<param>>.front_screw_height
  expr: Constraints[9] = <<param>>.face_offset + <<param>>.front_screw_offset
  sketch-geometry (6):
    g0: Circle CenterX=-36.75 CenterY=32.3 CenterZ=0 NormalX=0 NormalY=0 NormalZ=1 AngleXU=0 Radius=1.25
    g1: Circle CenterX=36.75 CenterY=32.3 CenterZ=0 NormalX=0 NormalY=0 NormalZ=1 AngleXU=0 Radius=1.25
    g2: Circle CenterX=-38 CenterY=8.3 CenterZ=0 NormalX=0 NormalY=0 NormalZ=1 AngleXU=0 Radius=1.25
    g3: Circle CenterX=38 CenterY=8.3 CenterZ=0 NormalX=0 NormalY=0 NormalZ=1 AngleXU=0 Radius=1.25
    g4: LineSegment [constr] StartX=-36.75 StartY=32.3 StartZ=0 EndX=36.75 EndY=32.3 EndZ=0
    g5: LineSegment [constr] StartX=-38 StartY=8.3 StartZ=0 EndX=38 EndY=8.3 EndZ=0
  constraints (14):
    c: DistanceX(g0,g1) = 73.5
    c: DistanceX(g2,g3) = 76
    c: DistanceY(g3,g1) = 24
    c: Coincident(g4,g0)
    c: Coincident(g4,g1)
    c: Coincident(g5,g2)
    c: Coincident(g5,g3)
    c: Symmetric(g2,g3,g-2)
    c: Symmetric(g0,g1,g-2)
    c: DistanceY(g-1,g3) = 8.3
    c: Equal(g0,g2)
    c: Equal(g2,g3)
    c: Equal(g3,g1)
    c: Diameter(g0) = 2.5
FEATURE [Sketcher::SketchObject] Sketch027  label="SketchButtonCarve"
  ArcFitTolerance = 0
  AttachmentOffset = pos=(10,22,0) rot=(0,0,1;-0.296706rad)
  AttachmentSupport = -> [YZ_Plane005]
  FullyConstrained = true
  MapMode = 5
  Placement = pos=(-2.7e-15,10,22) rot=(-0.51122,-0.690875,-0.51122;4.35074rad)
  Support = -> [YZ_Plane005]
  TreeRank = 0
  expr: AttachmentOffset.Base.x = <<param>>.button_offset
  expr: AttachmentOffset.Base.y = <<param>>.button_height - 2
  expr: AttachmentOffset.Rotation.Angle = <<param>>.button_angle
  expr: Constraints[12] = <<param>>.button_hole / 2 + 10
  expr: Constraints[6] = <<param>>.button_hole / 2 + 4
  sketch-geometry (4):
    g0: LineSegment StartX=0 StartY=2 StartZ=0 EndX=12.2 EndY=2 EndZ=0
    g1: ArcOfCircle CenterX=18.2 CenterY=3.09999 CenterZ=0 NormalX=0 NormalY=0 NormalZ=1 AngleXU=0 Radius=6.09999 StartAngle=3.32291 EndAngle=4.71239
    g2: LineSegment StartX=0 StartY=2 StartZ=0 EndX=0 EndY=-3 EndZ=0
    g3: LineSegment StartX=18.2 StartY=-3 StartZ=0 EndX=0 EndY=-3 EndZ=0
  constraints (13):
    c: Horizontal(g0)
    c: Coincident(g1,g0)
    c: Coincident(g2,g0)
    c: Coincident(g3,g1)
    c: Horizontal(g3)
    c: Tangent(g3,g1)
    c: DistanceX(g0,g0) = 12.2
    c: DistanceY(g2,g2) = 5
    c: Coincident(g2,g3)
    c: Vertical(g2)
    c: PointOnObject(g-1,g2)
    c: DistanceY(g2,g-1) = 3
    c: DistanceX(g3,g3) = 18.2
FEATURE [Sketcher::SketchObject] Sketch028  label="SketchTerminals"
  ArcFitTolerance = 0
  AttachmentSupport = -> [XZ_Plane005]
  FullyConstrained = true
  MapMode = 5
  Placement = pos=(0,0,0) rot=(1,0,0;1.5708rad)
  Support = -> [XZ_Plane005]
  TreeRank = 0
  expr: Constraints[17] = <<param>>.terminal_thickness
  expr: Constraints[18] = <<param>>.terminal_height
  expr: Constraints[21] = <<param>>.bottom_height
  expr: Constraints[22] = <<param>>.terminal_offset
  expr: Constraints[23] = <<param>>.terminal_seperation
  sketch-geometry (17):
    g0: LineSegment StartX=10.25 StartY=-12.9 StartZ=0 EndX=11.25 EndY=-12.9 EndZ=0
    g1: LineSegment StartX=11.25 StartY=-12.9 StartZ=0 EndX=11.25 EndY=-19.5 EndZ=0
    g2: LineSegment StartX=11.25 StartY=-19.5 StartZ=0 EndX=10.25 EndY=-19.5 EndZ=0
    g3: LineSegment StartX=10.25 StartY=-19.5 StartZ=0 EndX=10.25 EndY=-17.25 EndZ=0
    g4: LineSegment StartX=-10.25 StartY=-12.9 StartZ=0 EndX=-11.25 EndY=-12.9 EndZ=0
    g5: LineSegment StartX=-11.25 StartY=-12.9 StartZ=0 EndX=-11.25 EndY=-19.5 EndZ=0
    g6: LineSegment StartX=-11.25 StartY=-19.5 StartZ=0 EndX=-10.25 EndY=-19.5 EndZ=0
    g7: LineSegment StartX=-10.25 StartY=-19.5 StartZ=0 EndX=-10.25 EndY=-17.25 EndZ=0
    g8: Circle [constr] CenterX=0 CenterY=-24 CenterZ=0 NormalX=0 NormalY=0 NormalZ=1 AngleXU=0 Radius=3
    g9: LineSegment StartX=-10.25 StartY=-15.15 StartZ=0 EndX=-8.75 EndY=-15.15 EndZ=0
    g10: LineSegment StartX=-10.25 StartY=-17.25 StartZ=0 EndX=-8.75 EndY=-17.25 EndZ=0
    g11: LineSegment StartX=-8.75 StartY=-15.15 StartZ=0 EndX=-8.75 EndY=-17.25 EndZ=0
    g12: LineSegment StartX=10.25 StartY=-15.15 StartZ=0 EndX=8.75 EndY=-15.15 EndZ=0
    g13: LineSegment StartX=8.75 StartY=-15.15 StartZ=0 EndX=8.75 EndY=-17.25 EndZ=0
    g14: LineSegment StartX=8.75 StartY=-17.25 StartZ=0 EndX=10.25 EndY=-17.25 EndZ=0
    g15: LineSegment StartX=-10.25 StartY=-15.15 StartZ=0 EndX=-10.25 EndY=-12.9 EndZ=0
    g16: LineSegment StartX=10.25 StartY=-15.15 StartZ=0 EndX=10.25 EndY=-12.9 EndZ=0
  constraints (48):
    c: Coincident(g0,g1)
    c: Coincident(g1,g2)
    c: Coincident(g2,g3)
    c: Coincident(g16,g0)
    c: Horizontal(g0)
    c: Horizontal(g2)
    c: Vertical(g1)
    c: Vertical(g3)
    c: Coincident(g4,g5)
    c: Coincident(g5,g6)
    c: Coincident(g6,g7)
    c: Coincident(g15,g4)
    c: Horizontal(g4)
    c: Horizontal(g6)
    c: Vertical(g5)
    c: Vertical(g7)
    c: Equal(g4,g0)
    c: DistanceX(g4,g4) = 1
    c: DistanceY(g3,g16) = 6.6
    c: PointOnObject(g8,g-2)
    c: Radius(g8) = 3
    c: DistanceY(g8,g-1) = 24
    c: DistanceY(g8,g1) = 4.5
    c: DistanceX(g6,g1) = 21.5
    c: Symmetric(g4,g0,g-2)
    c: Horizontal(g9)
    c: Horizontal(g10)
    c: Coincident(g11,g9)
    c: Coincident(g11,g10)
    c: Vertical(g11)
    c: Horizontal(g12)
    c: Coincident(g13,g12)
    c: Vertical(g13)
    c: Coincident(g14,g13)
    c: Horizontal(g14)
    c: Coincident(g7,g10)
    c: Coincident(g15,g9)
    c: Tangent(g7,g15)
    c: Coincident(g3,g14)
    c: Coincident(g16,g12)
    c: Tangent(g3,g16)
    c: Equal(g15,g7)
    c: Equal(g7,g3)
    c: Equal(g3,g16)
    c: Equal(g10,g14)
    c: Equal(g11,g13)
    c: DistanceY(g11,g11) = 2.1
    c: DistanceX(g12,g12) = 1.5
FEATURE [Sketcher::SketchObject] Sketch029  label="SketchAccess"
  ArcFitTolerance = 0
  AttachmentOffset = pos=(0,0,-20.5) rot=(0,0,1;0rad)
  AttachmentSupport = -> [XY_Plane005]
  FullyConstrained = true
  MapMode = 5
  Placement = pos=(0,0,-20.5) rot=(0,0,1;0rad)
  Support = -> [XY_Plane005]
  TreeRank = 0
  expr: AttachmentOffset.Base.z = -<<param>>.bottom_height + <<param>>.terminal_offset - 1
  expr: Constraints[20] = <<param>>.mid_depth / 2
  expr: Constraints[9] = <<param>>.terminal_seperation + <<param>>.terminal_thickness * 2
  sketch-geometry (12):
    g0: LineSegment StartX=-11.75 StartY=41 StartZ=0 EndX=-11.75 EndY=18.5 EndZ=0
    g1: LineSegment StartX=-7.95 StartY=41 StartZ=0 EndX=-7.95 EndY=21 EndZ=0
    g2: LineSegment StartX=7.95 StartY=41 StartZ=0 EndX=7.95 EndY=21 EndZ=0
    g3: LineSegment StartX=11.75 StartY=41 StartZ=0 EndX=11.75 EndY=18.5 EndZ=0
    g4: LineSegment StartX=-11.75 StartY=41 StartZ=0 EndX=-7.95 EndY=41 EndZ=0
    g5: LineSegment StartX=7.95 StartY=41 StartZ=0 EndX=11.75 EndY=41 EndZ=0
    g6: LineSegment StartX=-11.75 StartY=18.5 StartZ=0 EndX=-9.25 EndY=18.5 EndZ=0
    g7: LineSegment StartX=11.75 StartY=18.5 StartZ=0 EndX=9.25 EndY=18.5 EndZ=0
    g8: LineSegment StartX=-9.25 StartY=18.5 StartZ=0 EndX=-9.25 EndY=19.5 EndZ=0
    g9: LineSegment StartX=-9.25 StartY=19.5 StartZ=0 EndX=-7.95 EndY=21 EndZ=0
    g10: LineSegment StartX=9.25 StartY=18.5 StartZ=0 EndX=9.25 EndY=19.5 EndZ=0
    g11: LineSegment StartX=9.25 StartY=19.5 StartZ=0 EndX=7.95 EndY=21 EndZ=0
  constraints (35):
    c: Vertical(g0)
    c: Vertical(g2)
    c: Equal(g1,g2)
    c: Coincident(g4,g0)
    c: Coincident(g4,g1)
    c: Horizontal(g4)
    c: Coincident(g5,g2)
    c: Coincident(g5,g3)
    c: Horizontal(g5)
    c: DistanceX(g0,g3) = 23.5
    c: Vertical(g3)
    c: Equal(g5,g4)
    c: Symmetric(g1,g2,g-2)
    c: DistanceX(g4,g4) = 3.8
    c: Vertical(g1)
    c: Equal(g0,g3)
    c: Coincident(g6,g0)
    c: Horizontal(g6)
    c: Coincident(g7,g3)
    c: Equal(g6,g7)
    c: DistanceY(g-1,g3) = 41
    c: Horizontal(g7)
    c: Coincident(g8,g6)
    c: Vertical(g8)
    c: Coincident(g9,g8)
    c: Coincident(g9,g1)
    c: Coincident(g10,g7)
    c: Coincident(g11,g10)
    c: Coincident(g11,g2)
    c: Equal(g8,g10)
    c: Equal(g9,g11)
    c: DistanceY(g1,g1) = 20
    c: DistanceY(g0,g0) = 22.5
    c: DistanceX(g6,g6) = 2.5
    c: DistanceY(g8,g8) = 1
FEATURE [Sketcher::SketchObject] Sketch030  label="SketchFront"
  ArcFitTolerance = 0
  AttachmentOffset = pos=(0,0,41) rot=(0,0,1;0rad)
  AttachmentSupport = -> [XZ_Plane006]
  FullyConstrained = true
  MapMode = 5
  Placement = pos=(0,-41,-9.1e-15) rot=(1,0,0;1.5708rad)
  Support = -> [XZ_Plane006]
  TreeRank = 0
  expr: AttachmentOffset.Base.z = <<param>>.mid_depth / 2
  expr: Constraints[10] = <<param>>.front_width2
  expr: Constraints[11] = <<param>>.front_width2
  expr: Constraints[12] = <<param>>.front_height + 2
  expr: Constraints[24] = <<param>>.radius_big * 1.2
  expr: Constraints[25] = <<param>>.radius_big
  expr: Constraints[6] = <<param>>.radius_small
  expr: Constraints[7] = <<param>>.bottom_width
  expr: Constraints[9] = <<param>>.bottom_height
  sketch-geometry (12):
    g0: LineSegment StartX=-47 StartY=42 StartZ=0 EndX=47 EndY=42 EndZ=0
    g1: LineSegment StartX=47 StartY=42 StartZ=0 EndX=47 EndY=9.3923 EndZ=0
    g2: LineSegment StartX=36 StartY=-9.66025 StartZ=0 EndX=36 EndY=-21 EndZ=0
    g3: LineSegment StartX=33 StartY=-24 StartZ=0 EndX=-33 EndY=-24 EndZ=0
    g4: LineSegment StartX=-36 StartY=-21 StartZ=0 EndX=-36 EndY=-9.66025 EndZ=0
    g5: LineSegment StartX=-47 StartY=9.3923 StartZ=0 EndX=-47 EndY=42 EndZ=0
    g6: ArcOfCircle CenterX=-33 CenterY=-21 CenterZ=0 NormalX=0 NormalY=0 NormalZ=1 AngleXU=0 Radius=3 StartAngle=3.14159 EndAngle=4.71239
    g7: ArcOfCircle CenterX=33 CenterY=-21 CenterZ=0 NormalX=0 NormalY=0 NormalZ=1 AngleXU=0 Radius=3 StartAngle=4.71239 EndAngle=6.28319
    g8: ArcOfCircle CenterX=46 CenterY=-9.66025 CenterZ=0 NormalX=0 NormalY=0 NormalZ=1 AngleXU=0 Radius=10 StartAngle=2.0944 EndAngle=3.14159
    g9: ArcOfCircle CenterX=35 CenterY=9.3923 CenterZ=0 NormalX=0 NormalY=0 NormalZ=1 AngleXU=0 Radius=12 StartAngle=5.23599 EndAngle=6.28319
    g10: ArcOfCircle CenterX=-46 CenterY=-9.66025 CenterZ=0 NormalX=0 NormalY=0 NormalZ=1 AngleXU=0 Radius=10 StartAngle=0 EndAngle=1.0472
    g11: ArcOfCircle CenterX=-35 CenterY=9.3923 CenterZ=0 NormalX=0 NormalY=0 NormalZ=1 AngleXU=0 Radius=12 StartAngle=3.14159 EndAngle=4.18879
  constraints (30):
    c: Vertical(g2)
    c: Vertical(g4)
    c: Tangent(g4,g6) = 1.5708
    c: Tangent(g3,g6) = 1.5708
    c: Tangent(g3,g7) = 1.5708
    c: Tangent(g2,g7) = 1.5708
    c: Radius(g7) = 3
    c: DistanceX(g4,g2) = 72
    c: Symmetric(g3,g3,g-2)
    c: DistanceY(g3,g-1) = 24
    c: DistanceX(g5,g1) = 94
    c: DistanceX(g5,g1) = 94
    c: DistanceY(g3,g0) = 66
    c: Equal(g7,g6)
    c: Symmetric(g5,g1,g-2)
    c: Equal(g4,g2)
    c: Coincident(g0,g1)
    c: Coincident(g5,g0)
    c: Symmetric(g0,g0,g-2)
    c: Tangent(g10,g4) = -1.5708
    c: Tangent(g8,g2) = -1.5708
    c: Coincident(g11,g10)
    c: DistanceY(g8,g-1) = 1
    c: Equal(g9,g11)
    c: Radius(g9) = 12
    c: Radius(g8) = 10
    c: Equal(g8,g10)
    c: Tangent(g11,g5) = 1.5708
    c: Tangent(g1,g9) = 1.5708
    c: Tangent(g8,g9) = 1.5708
FEATURE [Sketcher::SketchObject] Sketch031  label="SketchRear"
  ArcFitTolerance = 0
  AttachmentOffset = pos=(0,0,-46) rot=(0,0,1;0rad)
  AttachmentSupport = -> [XZ_Plane006]
  FullyConstrained = true
  MapMode = 5
  Placement = pos=(0,46,1.02e-14) rot=(1,0,0;1.5708rad)
  Support = -> [XZ_Plane006]
  TreeRank = 0
  expr: AttachmentOffset.Base.z = -<<param>>.mid_depth / 2 - <<param>>.back_thickness
  expr: Constraints[15] = <<param>>.front_height + 2
  expr: Constraints[1] = <<param>>.radius_small
  expr: Constraints[2] = <<param>>.bottom_height
  expr: Constraints[3] = <<param>>.rear_width
  sketch-geometry (6):
    g0: LineSegment StartX=-33 StartY=-24 StartZ=0 EndX=33 EndY=-24 EndZ=0
    g1: LineSegment StartX=36 StartY=42 StartZ=0 EndX=-36 EndY=42 EndZ=0
    g2: ArcOfCircle CenterX=-33 CenterY=-21 CenterZ=0 NormalX=0 NormalY=0 NormalZ=1 AngleXU=0 Radius=3 StartAngle=3.14159 EndAngle=4.71239
    g3: ArcOfCircle CenterX=33 CenterY=-21 CenterZ=0 NormalX=0 NormalY=0 NormalZ=1 AngleXU=0 Radius=3 StartAngle=4.71239 EndAngle=6.28319
    g4: LineSegment StartX=36 StartY=-21 StartZ=0 EndX=36 EndY=42 EndZ=0
    g5: LineSegment StartX=-36 StartY=-21 StartZ=0 EndX=-36 EndY=42 EndZ=0
  constraints (19):
    c: Horizontal(g0)
    c: Radius(g3) = 3
    c: DistanceY(g0,g-1) = 24
    c: DistanceX(g2,g3) = 72
    c: Coincident(g4,g3)
    c: Vertical(g4)
    c: Coincident(g5,g2)
    c: Equal(g5,g4)
    c: Horizontal(g3,g3)
    c: Horizontal(g2,g2)
    c: Equal(g2,g3)
    c: Coincident(g0,g2)
    c: Coincident(g0,g3)
    c: Vertical(g2,g0)
    c: Vertical(g5)
    c: DistanceY(g0,g1) = 66
    c: Symmetric(g4,g5,g-2)
    c: Coincident(g4,g1)
    c: Coincident(g5,g1)
FEATURE [Part::Plane] Plane002  label="Plane"
  AttacherType = Attacher::AttachEngine3D
  AttachmentSupport = -> [XZ_Plane006]
  Length = 152
  Placement = pos=(-75,41,-75) rot=(1,0,0;1.5708rad)
  Support = -> [XZ_Plane006]
  TreeRank = 0
  Width = 150
  expr: Placement.Base.y = <<param>>.mid_depth / 2
FEATURE [Sketcher::SketchObject] Sketch032  label="SketchBack"
  ArcFitTolerance = 0
  AttachmentSupport = -> [XZ_Plane]
  FullyConstrained = true
  MapMode = 5
  Placement = pos=(0,0,0) rot=(1,0,0;1.5708rad)
  Support = -> [XZ_Plane]
  TreeRank = 0
  expr: Constraints[10] = <<param>>.rear_screw_width1
  expr: Constraints[11] = <<param>>.reart_screw_width2
  expr: Constraints[12] = <<param>>.rear_screw_height
  expr: Constraints[15] = <<param>>.rear_screw_offset
  expr: Constraints[1] = <<param>>.bottom_height
  expr: Constraints[2] = <<param>>.rear_width
  expr: Constraints[9] = <<param>>.screw_hole + 1
  sketch-geometry (6):
    g0: LineSegment [constr] StartX=36 StartY=-24 StartZ=0 EndX=-36 EndY=-24 EndZ=0
    g1: Circle CenterX=-29 CenterY=8.9 CenterZ=0 NormalX=0 NormalY=0 NormalZ=1 AngleXU=0 Radius=1.75
    g2: Circle CenterX=0 CenterY=8.9 CenterZ=0 NormalX=0 NormalY=0 NormalZ=1 AngleXU=0 Radius=1.75
    g3: Circle CenterX=29 CenterY=8.9 CenterZ=0 NormalX=0 NormalY=0 NormalZ=1 AngleXU=0 Radius=1.75
    g4: Circle CenterX=-27.5 CenterY=-16.6 CenterZ=0 NormalX=0 NormalY=0 NormalZ=1 AngleXU=0 Radius=1.75
    g5: Circle CenterX=27.5 CenterY=-16.6 CenterZ=0 NormalX=0 NormalY=0 NormalZ=1 AngleXU=0 Radius=1.75
  constraints (16):
    c: Symmetric(g0,g0,g-2)
    c: DistanceY(g0,g-1) = 24
    c: DistanceX(g0,g0) = 72
    c: Symmetric(g1,g3,g-2)
    c: Symmetric(g4,g5,g-2)
    c: Equal(g4,g1)
    c: Equal(g1,g2)
    c: Equal(g2,g3)
    c: Equal(g3,g5)
    c: Diameter(g1) = 3.5
    c: DistanceX(g1,g3) = 58
    c: DistanceX(g4,g5) = 55
    c: DistanceY(g5,g3) = 25.5
    c: Horizontal(g1,g2)
    c: PointOnObject(g2,g-2)
    c: DistanceY(g0,g5) = 7.4
FEATURE [Part::Loft] Loft
  Closed = false
  MaxDegree = 5
  Ruled = false
  Sections = -> [Sketch030,Sketch031]
  Solid = true
  TreeRank = 0
FEATURE [Part::Extrusion] Extrude
  Base = -> Sketch012
  Dir = (1,-1e-16,1e-16)
  DirMode = 2
  FaceMakerClass = Part::FaceMakerBullseye
  InnerTaperAngle = 0
  InnerTaperAngleRev = 0
  LengthFwd = 100
  LengthRev = 0
  Solid = true
  Symmetric = true
  TreeRank = 0
FEATURE [Part::MultiCommon] Common
  Shapes = -> [Extrude,Loft]
  TreeRank = 0
FEATURE [Part::FeaturePython] Slice  # WARN: FeaturePython — macro-defined, semantics opaque (R4)
  Base = -> Common
  Mode = 1
  Tolerance = 0
  Tools = -> [Plane002]
  TreeRank = 0
FEATURE [Part::FeaturePython] Slice_child0  label="Slice.0"  # WARN: FeaturePython — macro-defined, semantics opaque (R4)
  Base = -> Slice
  FilterType = 1
  Invert = false
  OverrideMaxVal = 0
  TreeRank = 0
  WindowFrom = 80
  WindowTo = 100
  items = 0
FEATURE [Part::FeaturePython] Slice_child1  label="Slice.1"  # WARN: FeaturePython — macro-defined, semantics opaque (R4)
  Base = -> Slice
  FilterType = 1
  Invert = false
  OverrideMaxVal = 0
  TreeRank = 0
  WindowFrom = 80
  WindowTo = 100
  items = 1
FEATURE [App::DocumentObjectGroup] GrExplode_Slice  label="Exploded Slice"
  ClaimAllChildren = true
  ExportMode = 1
  Group = -> [Slice_child0,Slice_child1]
  TreeRank = 0
  _GroupVersion = 1
FEATURE [App::DocumentObjectGroup] Group001  label="BaseShape"
  ClaimAllChildren = true
  ExportMode = 1
  Group = -> [Common,Sketch012,Sketch031,Sketch030,Plane002,GrExplode_Slice]
  TreeRank = 0
  _GroupVersion = 1
FEATURE [PartDesign::FeatureBase] BaseFeature
  BaseFeature = -> Slice_child1
  NewSolid = false
  Suppress = false
  TreeRank = 0
FEATURE [PartDesign::Pocket] Pocket
  BaseFeature = -> BaseFeature
  ClaimChildren = false
  Fit = 0
  FitJoin = 0
  InnerFit = 0
  InnerFitJoin = 0
  InnerTaperAngle = 0
  InnerTaperAngleRev = 0
  Length = 5
  Length2 = 100
  Midplane = true
  NewSolid = false
  Profile = -> Sketch032
  Suppress = false
  TreeRank = 0
  Type = 1
  _ProfileBasedVersion = 0
FEATURE [PartDesign::Fillet] Fillet
  Base = -> Pocket [Edge30,Edge63]
  BaseFeature = -> Pocket
  NewSolid = false
  Radius = 10
  SupportTransform = false
  Suppress = false
  TreeRank = 0
  expr: Radius = <<param>>.radius_big
FEATURE [PartDesign::FeatureBase] BaseFeature001
  BaseFeature = -> Slice_child0
  NewSolid = false
  Suppress = false
  TreeRank = 0
FEATURE [PartDesign::Pocket] Pocket001  label="PocketBatt"
  BaseFeature = -> BaseFeature001
  ClaimChildren = false
  Fit = 0
  FitJoin = 0
  InnerFit = 0
  InnerFitJoin = 0
  InnerTaperAngle = 0
  InnerTaperAngleRev = 0
  Length = 14.6
  Length2 = 100
  NewSolid = false
  Profile = -> Sketch018
  Reversed = true
  Suppress = false
  TreeRank = 0
  Type = 0
  _ProfileBasedVersion = 0
  expr: Length = <<param>>.batt_carveout
FEATURE [PartDesign::Pad] Pad  label="PadBatt"
  BaseFeature = -> Pocket001
  ClaimChildren = false
  Direction = (1,1,1)
  Fit = 0
  FitJoin = 0
  InnerFit = 0
  InnerFitJoin = 0
  InnerTaperAngle = 0
  InnerTaperAngleRev = 0
  Length = 45
  Length2 = 100
  NewSolid = false
  Profile = -> Sketch019
  Suppress = false
  TreeRank = 0
  Type = 0
  _ProfileBasedVersion = 0
  expr: Length = <<param>>.batt_rail_length
FEATURE [PartDesign::Pocket] Pocket002  label="PocketSupport"
  BaseFeature = -> Pad
  ClaimChildren = false
  Fit = 0
  FitJoin = 0
  InnerFit = 0
  InnerFitJoin = 0
  InnerTaperAngle = 0
  InnerTaperAngleRev = 0
  Length = 5
  Length2 = 100
  NewSolid = false
  Profile = -> Sketch
  Suppress = false
  TreeRank = 0
  Type = 0
  _ProfileBasedVersion = 0
FEATURE [PartDesign::Pocket] Pocket006  label="PocketTerminal"
  BaseFeature = -> Pocket002
  ClaimChildren = false
  Fit = 0
  FitJoin = 0
  InnerFit = 0
  InnerFitJoin = 0
  InnerTaperAngle = 0
  InnerTaperAngleRev = 0
  Length = 18.5
  Length2 = 100
  NewSolid = false
  Profile = -> Sketch028
  Suppress = false
  TreeRank = 0
  Type = 0
  _ProfileBasedVersion = 0
  expr: Length = <<param>>.mid_depth / 2 - <<param>>.terminal_depth
FEATURE [PartDesign::Pocket] Pocket005  label="PocketAccess"
  BaseFeature = -> Pocket006
  ClaimChildren = false
  Fit = 0
  FitJoin = 0
  InnerFit = 0
  InnerFitJoin = 0
  InnerTaperAngle = 0
  InnerTaperAngleRev = 0
  Length = 22.5
  Length2 = 100
  NewSolid = false
  Profile = -> Sketch029
  Reversed = true
  Suppress = false
  TreeRank = 0
  Type = 0
  _ProfileBasedVersion = 0
  expr: Length = <<param>>.terminal_depth
FEATURE [Sketcher::SketchObject] Sketch033  label="SketchFace"
  ArcFitTolerance = 0
  AttachmentOffset = pos=(0,0,38) rot=(1,0,0;-0.349066rad)
  AttachmentSupport = -> [XZ_Plane007]
  FullyConstrained = true
  MapMode = 5
  Placement = pos=(0,-38,-8.4e-15) rot=(-1,0,0;5.06145rad)
  Support = -> [XZ_Plane007]
  TreeRank = 0
  expr: AttachmentOffset.Base.z = <<param>>.mid_depth / 2 - <<param>>.face_thickness
  expr: AttachmentOffset.Rotation.Angle = -<<param>>.front_angle
  expr: Constraints[12] = <<param>>.face_radius
  expr: Constraints[21] = <<param>>.face_width1 - 0.2
  expr: Constraints[22] = <<param>>.face_width2 - 0.2
  expr: Constraints[23] = <<param>>.face_height - 0.2
  expr: Constraints[27] = <<param>>.screw_hole + 1
  expr: Constraints[28] = <<param>>.front_screw_width2 / 2
  expr: Constraints[29] = <<param>>.front_screw_width2 / 2
  expr: Constraints[30] = <<param>>.front_screw_width1 / 2
  expr: Constraints[31] = <<param>>.front_screw_width1 / 2
  expr: Constraints[32] = <<param>>.front_screw_height
  expr: Constraints[35] = <<param>>.front_screw_offset + <<param>>.face_offset
  expr: Constraints[48] = <<param>>.face_offset
  sketch-geometry (25):
    g0: LineSegment StartX=-34.4064 StartY=37.6 StartZ=0 EndX=34.4064 EndY=37.6 EndZ=0
    g1: LineSegment StartX=42.4 StartY=29.9189 StartZ=0 EndX=43.15 EndY=11.1189 EndZ=0
    g2: LineSegment StartX=35.1564 StartY=2.8 StartZ=0 EndX=-35.1564 EndY=2.8 EndZ=0
    g3: LineSegment StartX=-43.15 StartY=11.1189 StartZ=0 EndX=-42.4 EndY=29.9189 EndZ=0
    g4: ArcOfCircle CenterX=34.4064 CenterY=29.6 CenterZ=0 NormalX=0 NormalY=0 NormalZ=1 AngleXU=0 Radius=8 StartAngle=0.0398724 EndAngle=1.5708
    g5: ArcOfCircle CenterX=35.1564 CenterY=10.8 CenterZ=0 NormalX=0 NormalY=0 NormalZ=1 AngleXU=0 Radius=8 StartAngle=4.71239 EndAngle=6.32306
    g6: ArcOfCircle CenterX=-34.4064 CenterY=29.6 CenterZ=0 NormalX=0 NormalY=0 NormalZ=1 AngleXU=0 Radius=8 StartAngle=1.5708 EndAngle=3.10172
    g7: ArcOfCircle CenterX=-35.1564 CenterY=10.8 CenterZ=0 NormalX=0 NormalY=0 NormalZ=1 AngleXU=0 Radius=8 StartAngle=3.10172 EndAngle=4.71239
    g8: Circle CenterX=-36.75 CenterY=32.3 CenterZ=0 NormalX=0 NormalY=0 NormalZ=1 AngleXU=0 Radius=1.75
    g9: Circle CenterX=36.75 CenterY=32.3 CenterZ=0 NormalX=0 NormalY=0 NormalZ=1 AngleXU=0 Radius=1.75
    g10: Circle CenterX=-38 CenterY=8.3 CenterZ=0 NormalX=0 NormalY=0 NormalZ=1 AngleXU=0 Radius=1.75
    g11: Circle CenterX=38 CenterY=8.3 CenterZ=0 NormalX=0 NormalY=0 NormalZ=1 AngleXU=0 Radius=1.75
    g12: LineSegment StartX=-11.75 StartY=28.5 StartZ=0 EndX=7.75 EndY=28.5 EndZ=0
    g13: LineSegment StartX=10 StartY=26.25 StartZ=0 EndX=10 EndY=17.65 EndZ=0
    g14: LineSegment StartX=7.75 StartY=15.4 StartZ=0 EndX=-11.75 EndY=15.4 EndZ=0
    g15: LineSegment StartX=-14 StartY=17.65 StartZ=0 EndX=-14 EndY=26.25 EndZ=0
    g16: ArcOfCircle CenterX=-11.75 CenterY=26.25 CenterZ=0 NormalX=0 NormalY=0 NormalZ=1 AngleXU=0 Radius=2.25 StartAngle=1.5708 EndAngle=3.14159
    g17: ArcOfCircle CenterX=-11.75 CenterY=17.65 CenterZ=0 NormalX=0 NormalY=0 NormalZ=1 AngleXU=0 Radius=2.25 StartAngle=3.14159 EndAngle=4.71239
    g18: ArcOfCircle CenterX=7.75 CenterY=17.65 CenterZ=0 NormalX=0 NormalY=0 NormalZ=1 AngleXU=0 Radius=2.25 StartAngle=4.71239 EndAngle=6.28319
    g19: ArcOfCircle CenterX=7.75 CenterY=26.25 CenterZ=0 NormalX=0 NormalY=0 NormalZ=1 AngleXU=0 Radius=2.25 StartAngle=0 EndAngle=1.5708
    g20: Circle CenterX=25 CenterY=22.9 CenterZ=0 NormalX=0 NormalY=0 NormalZ=1 AngleXU=0 Radius=3.7
    g21: LineSegment StartX=-29.35 StartY=25.9392 StartZ=0 EndX=-24.65 EndY=25.9392 EndZ=0
    g22: LineSegment StartX=-29.35 StartY=14.6808 StartZ=0 EndX=-24.65 EndY=14.6808 EndZ=0
    g23: ArcOfCircle CenterX=-27 CenterY=20.31 CenterZ=0 NormalX=0 NormalY=0 NormalZ=1 AngleXU=0 Radius=6.1 StartAngle=1.96627 EndAngle=4.31691
    g24: ArcOfCircle CenterX=-27 CenterY=20.31 CenterZ=0 NormalX=0 NormalY=0 NormalZ=1 AngleXU=0 Radius=6.1 StartAngle=5.10786 EndAngle=7.45851
  constraints (75):
    c: Coincident(g4,g0)
    c: Coincident(g4,g1)
    c: Coincident(g5,g1)
    c: Coincident(g5,g2)
    c: Coincident(g6,g0)
    c: Coincident(g6,g3)
    c: Coincident(g7,g3)
    c: Coincident(g7,g2)
    c: Equal(g1,g3)
    c: Equal(g4,g6)
    c: Equal(g6,g7)
    c: Equal(g7,g5)
    c: Radius(g4) = 8
    c: Tangent(g6,g3)
    c: Tangent(g7,g3)
    c: Tangent(g7,g2)
    c: Tangent(g6,g0)
    c: Tangent(g4,g0)
    c: Tangent(g4,g1)
    c: Tangent(g5,g1)
    c: Tangent(g5,g2)
    c: DistanceX(g3,g1) = 84.8
    c: DistanceX(g3,g1) = 86.3
    c: DistanceY(g2,g0) = 34.8
    c: Equal(g9,g8)
    c: Equal(g8,g10)
    c: Equal(g10,g11)
    c: Diameter(g8) = 3.5
    c: DistanceX(g10,g-1) = 38
    c: DistanceX(g-1,g11) = 38
    c: DistanceX(g-1,g9) = 36.75
    c: DistanceX(g8,g-1) = 36.75
    c: DistanceY(g11,g9) = 24
    c: Horizontal(g8,g9)
    c: Horizontal(g10,g11)
    c: DistanceY(g-1,g11) = 8.3
    c: Horizontal(g12)
    c: Horizontal(g14)
    c: Vertical(g13)
    c: Vertical(g15)
    c: Tangent(g15,g16) = 1.5708
    c: Tangent(g12,g16) = 1.5708
    c: Tangent(g15,g17) = 1.5708
    c: Tangent(g14,g17) = 1.5708
    c: Tangent(g14,g18) = 1.5708
    c: Tangent(g13,g18) = 1.5708
    c: Tangent(g12,g19) = 1.5708
    c: Tangent(g13,g19) = 1.5708
    c: DistanceY(g-1,g2) = 2.8
    c: Horizontal(g0)
    c: Symmetric(g2,g2,g-2)
    c: Radius(g20) = 3.7
    c: Distance(g20,g-2) = 25
    c: Distance(g20,g-1) = 22.9
    c: Distance(g12) = 19.5
    c: Distance(g15) = 8.6
    c: Distance(g15,g-2) = 14
    c: Distance(g14,g-1) = 15.4
    c: Radius(g19) = 2.25
    c: Equal(g19,g18)
    c: Equal(g18,g17)
    c: Equal(g17,g16)
    c: Horizontal(g21)
    c: Horizontal(g22)
    c: Equal(g21,g22)
    c: Coincident(g23,g21)
    c: Coincident(g23,g22)
    c: Coincident(g24,g23)
    c: Coincident(g24,g21)
    c: Coincident(g24,g22)
    c: Radius(g23) = 6.1
    c: Equal(g24,g23)
    c: Distance(g23,g-1) = 20.31
    c: Distance(g23,g-2) = 27
    c: Distance(g22) = 4.7
FEATURE [PartDesign::Pad] Pad001  label="PadFace"
  ClaimChildren = false
  Direction = (1,1,1)
  Fit = 0
  FitJoin = 0
  InnerFit = 0
  InnerFitJoin = 0
  InnerTaperAngle = 0
  InnerTaperAngleRev = 0
  Length = 3
  Length2 = 100
  NewSolid = false
  Placement = pos=(0,0,0) rot=(1,0,0;1.5708rad)
  Profile = -> Sketch033
  Suppress = false
  TreeRank = 0
  Type = 0
  _ProfileBasedVersion = 0
  expr: Length = <<param>>.face_thickness
FEATURE [PartDesign::Chamfer] Chamfer001
  Angle = 45
  Base = -> Pad001 [Edge34]
  BaseFeature = -> Pad001
  ChamferType = 0
  FlipDirection = false
  NewSolid = false
  Placement = pos=(0,0,0) rot=(1,0,0;1.5708rad)
  Size = 2
  Size2 = 1
  SupportTransform = false
  Suppress = false
  TreeRank = 0
FEATURE [PartDesign::Chamfer] Chamfer002
  Angle = 45
  Base = -> Chamfer001 [Edge62,Edge60,Edge61,Edge59]
  BaseFeature = -> Chamfer001
  ChamferType = 0
  FlipDirection = false
  NewSolid = false
  Placement = pos=(0,0,0) rot=(1,0,0;1.5708rad)
  Size = 1.4
  Size2 = 1
  SupportTransform = false
  Suppress = false
  TreeRank = 0
FEATURE [PartDesign::Body] Body005  label="BodyOLED"
  AutoGroupSolids = false
  ClaimAllChildren = false
  ExportMode = 0
  Group = -> [Sketch033,Pad001,Chamfer001,Chamfer002]
  Origin = -> Origin007
  Tip = -> Chamfer002
  TreeRank = 0
  _ExportChildren = -> [Pad001,Chamfer001,Chamfer002]
  _GroupVersion = 1
FEATURE [PartDesign::Fillet] Fillet009
  Base = -> Fillet [Edge8]
  BaseFeature = -> Fillet
  NewSolid = false
  Radius = 2.93
  SupportTransform = false
  Suppress = false
  TreeRank = 0
FEATURE [PartDesign::Chamfer] Chamfer
  Angle = 45
  Base = -> Fillet009 [Edge43,Edge44,Edge45,Edge71,Edge73]
  BaseFeature = -> Fillet009
  ChamferType = 0
  FlipDirection = false
  NewSolid = false
  Size = 1.4
  Size2 = 1
  SupportTransform = false
  Suppress = false
  TreeRank = 0
FEATURE [PartDesign::Body] Body  label="BodyBack"
  AutoGroupSolids = false
  BaseFeature = -> Slice_child1
  ClaimAllChildren = false
  ExportMode = 0
  Group = -> [BaseFeature,Sketch032,Pocket,Fillet,Fillet009,Chamfer]
  Origin = -> Origin
  Tip = -> Chamfer
  TreeRank = 0
  _ExportChildren = -> [BaseFeature,Pocket,Fillet,Fillet009,Chamfer]
  _GroupVersion = 1
FEATURE [Sketcher::SketchObject] Sketch034  label="SketchKey"
  ArcFitTolerance = 0
  AttachmentOffset = pos=(0,0,-41) rot=(0,0,1;0rad)
  AttachmentSupport = -> [XZ_Plane005]
  FullyConstrained = true
  MapMode = 5
  Placement = pos=(0,41,9.1e-15) rot=(1,0,0;1.5708rad)
  Support = -> [XZ_Plane005]
  TreeRank = 0
  expr: AttachmentOffset.Base.z = -<<param>>.mid_depth / 2
  expr: Constraints[21] = <<param>>.rear_screw_offset
  expr: Constraints[22] = <<param>>.reart_screw_width2
  expr: Constraints[23] = <<param>>.screw_hole / 2
  expr: Constraints[2] = <<param>>.bottom_height
  sketch-geometry (9):
    g0: Circle [constr] CenterX=0 CenterY=-24 CenterZ=0 NormalX=0 NormalY=0 NormalZ=1 AngleXU=0 Radius=3
    g1: LineSegment StartX=4.5 StartY=-24 StartZ=0 EndX=11.5 EndY=-24 EndZ=0
    g2: LineSegment StartX=11.5 StartY=-24 StartZ=0 EndX=11.5 EndY=-22.8 EndZ=0
    g3: LineSegment StartX=4.5 StartY=-24 StartZ=0 EndX=4.5 EndY=-22.8 EndZ=0
    g4: LineSegment StartX=5.5 StartY=-21.8 StartZ=0 EndX=10.5 EndY=-21.8 EndZ=0
    g5: ArcOfCircle CenterX=10.5 CenterY=-22.8 CenterZ=0 NormalX=0 NormalY=0 NormalZ=1 AngleXU=0 Radius=1 StartAngle=1.1e-15 EndAngle=1.5708
    g6: ArcOfCircle CenterX=5.5 CenterY=-22.8 CenterZ=0 NormalX=0 NormalY=0 NormalZ=1 AngleXU=0 Radius=1 StartAngle=1.5708 EndAngle=3.14159
    g7: Circle CenterX=-27.5 CenterY=-16.6 CenterZ=0 NormalX=0 NormalY=0 NormalZ=1 AngleXU=0 Radius=1.25
    g8: Circle CenterX=27.5 CenterY=-16.6 CenterZ=0 NormalX=0 NormalY=0 NormalZ=1 AngleXU=0 Radius=1.25
  constraints (26):
    c: PointOnObject(g0,g-2)
    c: Radius(g0) = 3
    c: DistanceY(g0,g-1) = 24
    c: Horizontal(g1)
    c: Coincident(g2,g1)
    c: Vertical(g2)
    c: Coincident(g3,g1)
    c: Horizontal(g4)
    c: Coincident(g5,g2)
    c: Coincident(g6,g3)
    c: Equal(g5,g6)
    c: Equal(g3,g2)
    c: Tangent(g6,g4) = 1.5708
    c: Tangent(g5,g4) = 1.5708
    c: Vertical(g3)
    c: DistanceX(g1,g1) = 7
    c: DistanceY(g1,g4) = 2.2
    c: DistanceX(g-1,g1) = 4.5
    c: Radius(g6) = 1
    c: Horizontal(g0,g1)
    c: Horizontal(g3,g6)
    c: DistanceY(g0,g7) = 7.4
    c: DistanceX(g7,g8) = 55
    c: Radius(g7) = 1.25
    c: Equal(g7,g8)
    c: Symmetric(g7,g8,g-2)
FEATURE [PartDesign::Pocket] Pocket008  label="PocketKey"
  BaseFeature = -> Pocket005
  ClaimChildren = false
  Fit = 0
  FitJoin = 0
  InnerFit = 0
  InnerFitJoin = 0
  InnerTaperAngle = 0
  InnerTaperAngleRev = 0
  Length = 0
  Length2 = 100
  Midplane = true
  NewSolid = false
  Profile = -> Sketch034
  Suppress = false
  TreeRank = 0
  Type = 3
  UpToFace = -> Pocket005 [Face26]
  _ProfileBasedVersion = 0
FEATURE [PartDesign::SubtractiveLoft] SubtractiveLoft
  BaseFeature = -> Pocket008
  ClaimChildren = false
  Closed = false
  Fit = 0
  FitJoin = 0
  InnerFit = 0
  InnerFitJoin = 0
  NewSolid = false
  Profile = -> Sketch022
  Ruled = true
  Sections = -> [Sketch025,Sketch023]
  Suppress = false
  TreeRank = 0
  _ProfileBasedVersion = 0
FEATURE [PartDesign::Revolution] Revolution  label="RevolutionButton"
  Angle = 360
  Axis = (-3e-16,0.292372,0.956305)
  Base = (-3.1e-15,10,24)
  BaseFeature = -> SubtractiveLoft
  ClaimChildren = false
  Fit = 0
  FitJoin = 0
  InnerFit = 0
  InnerFitJoin = 0
  NewSolid = false
  Profile = -> Sketch021
  ReferenceAxis = -> Sketch021 [V_Axis]
  Reversed = true
  Suppress = false
  TreeRank = 0
  _ProfileBasedVersion = 0
FEATURE [PartDesign::Pocket] Pocket007  label="PocketButton"
  BaseFeature = -> Revolution
  ClaimChildren = false
  Fit = 0
  FitJoin = 0
  InnerFit = 0
  InnerFitJoin = 0
  InnerTaperAngle = 0
  InnerTaperAngleRev = 0
  Length = 14
  Length2 = 100
  NewSolid = false
  Profile = -> Sketch008
  Reversed = true
  Suppress = false
  TreeRank = 0
  Type = 0
  _ProfileBasedVersion = 0
FEATURE [PartDesign::Groove] Groove  label="GrooveButton"
  Angle = 360
  Axis = (-3e-16,0.292372,0.956305)
  Base = (-2.7e-15,10,22)
  BaseFeature = -> Pocket007
  ClaimChildren = false
  Fit = 0
  FitJoin = 0
  InnerFit = 0
  InnerFitJoin = 0
  NewSolid = false
  Profile = -> Sketch027
  ReferenceAxis = -> Sketch027 [V_Axis]
  Suppress = false
  TreeRank = 0
  _ProfileBasedVersion = 0
FEATURE [PartDesign::Pocket] Pocket004  label="PocketFrontScrews"
  BaseFeature = -> Groove
  ClaimChildren = false
  Fit = 0
  FitJoin = 0
  InnerFit = 0
  InnerFitJoin = 0
  InnerTaperAngle = 0
  InnerTaperAngleRev = 0
  Length = 5
  Length2 = 100
  NewSolid = false
  Profile = -> Sketch026
  Suppress = false
  TreeRank = 0
  Type = 0
  _ProfileBasedVersion = 0
FEATURE [PartDesign::Pocket] Pocket003  label="PocketFace"
  BaseFeature = -> Pocket004
  ClaimChildren = false
  Fit = 0
  FitJoin = 0
  InnerFit = 0
  InnerFitJoin = 0
  InnerTaperAngle = 0
  InnerTaperAngleRev = 0
  Length = 3.1
  Length2 = 100
  NewSolid = false
  Profile = -> Sketch024
  Reversed = true
  Suppress = false
  TreeRank = 0
  Type = 0
  _ProfileBasedVersion = 0
  expr: Length = <<param>>.face_thickness + 0.1
FEATURE [PartDesign::Fillet] Fillet010  label="FilletButton"
  Base = -> Pocket003 [Edge199]
  BaseFeature = -> Pocket003
  NewSolid = false
  Radius = 10
  SupportTransform = false
  Suppress = false
  TreeRank = 0
FEATURE [PartDesign::Fillet] Fillet011  label="FilletBig"
  Base = -> Fillet010 [Edge2,Edge5]
  BaseFeature = -> Fillet010
  NewSolid = false
  Radius = 10
  SupportTransform = false
  Suppress = false
  TreeRank = 0
  expr: Radius = <<param>>.radius_big
FEATURE [PartDesign::Fillet] Fillet012  label="FilletFront"
  Base = -> Fillet011 [Edge11]
  BaseFeature = -> Fillet011
  NewSolid = false
  Radius = 2
  SupportTransform = false
  Suppress = false
  TreeRank = 0
FEATURE [PartDesign::Fillet] Fillet013  label="FilletFace"
  Base = -> Fillet012 [Edge57]
  BaseFeature = -> Fillet012
  NewSolid = false
  Radius = 2
  SupportTransform = false
  Suppress = false
  TreeRank = 0
FEATURE [PartDesign::Body] Body004  label="BodyCase"
  AutoGroupSolids = false
  BaseFeature = -> Slice_child0
  ClaimAllChildren = false
  ExportMode = 0
  Group = -> [BaseFeature001,Sketch008,Sketch029,Sketch018,Sketch019,Sketch021,Sketch022,Sketch023,Sketch024,Sketch025,Sketch026,Sketch027,Sketch028,Sketch,Pocket001,Pad,Pocket002,Pocket006,Pocket005,Pocket008,Sketch034,SubtractiveLoft,Revolution,Pocket007,Groove,Pocket004,Pocket003,Fillet010,Fillet011,Fillet012,Fillet013]
  Origin = -> Origin005
  Tip = -> Fillet013
  TreeRank = 0
  _ExportChildren = -> [BaseFeature001,Pocket001,Pad,Pocket002,Pocket006,Pocket005,Pocket008,SubtractiveLoft,Revolution,Pocket007,Groove,Pocket004,Pocket003,Fillet010,Fillet011,Fillet012,Fillet013]
  _GroupVersion = 1
FEATURE [Mesh::Feature] Mesh  label="BodyCase (Meshed)"
  TreeRank = 0
FEATURE [Mesh::Feature] Mesh001  label="BodyBack (Meshed)"
  TreeRank = 0
FEATURE [Mesh::Feature] T12Face
  Placement = pos=(0,-35,20.3) rot=(1,0,0;1.5708rad)
  TreeRank = 1
FEATURE [Mesh::Feature] Mesh002  label="BodyFace (Meshed)"
  TreeRank = 2
FEATURE [App::DocumentObjectGroup] Group002  label="Mesh"
  ClaimAllChildren = true
  ExportMode = 1
  Group = -> [Mesh001,Mesh,Mesh002,T12Face]
  TreeRank = 0
  _GroupVersion = 1
FEATURE [App::Part] Part
  ClaimAllChildren = false
  ExportMode = 1
  Group = -> [Extrude,Plane002,Common,Sketch012,Loft,Slice_child1,Slice_child0,Slice,GrExplode_Slice,Sketch030,Sketch031,Group001,Spreadsheet,Body,Body004,Body005,Group002,Mesh001,Mesh,Mesh002,T12Face]
  Origin = -> Origin006
  TreeRank = 0
  _ExportChildren = -> [Group001,Spreadsheet,Body,Body004,Body005,Group002]
  _GroupVersion = 1
